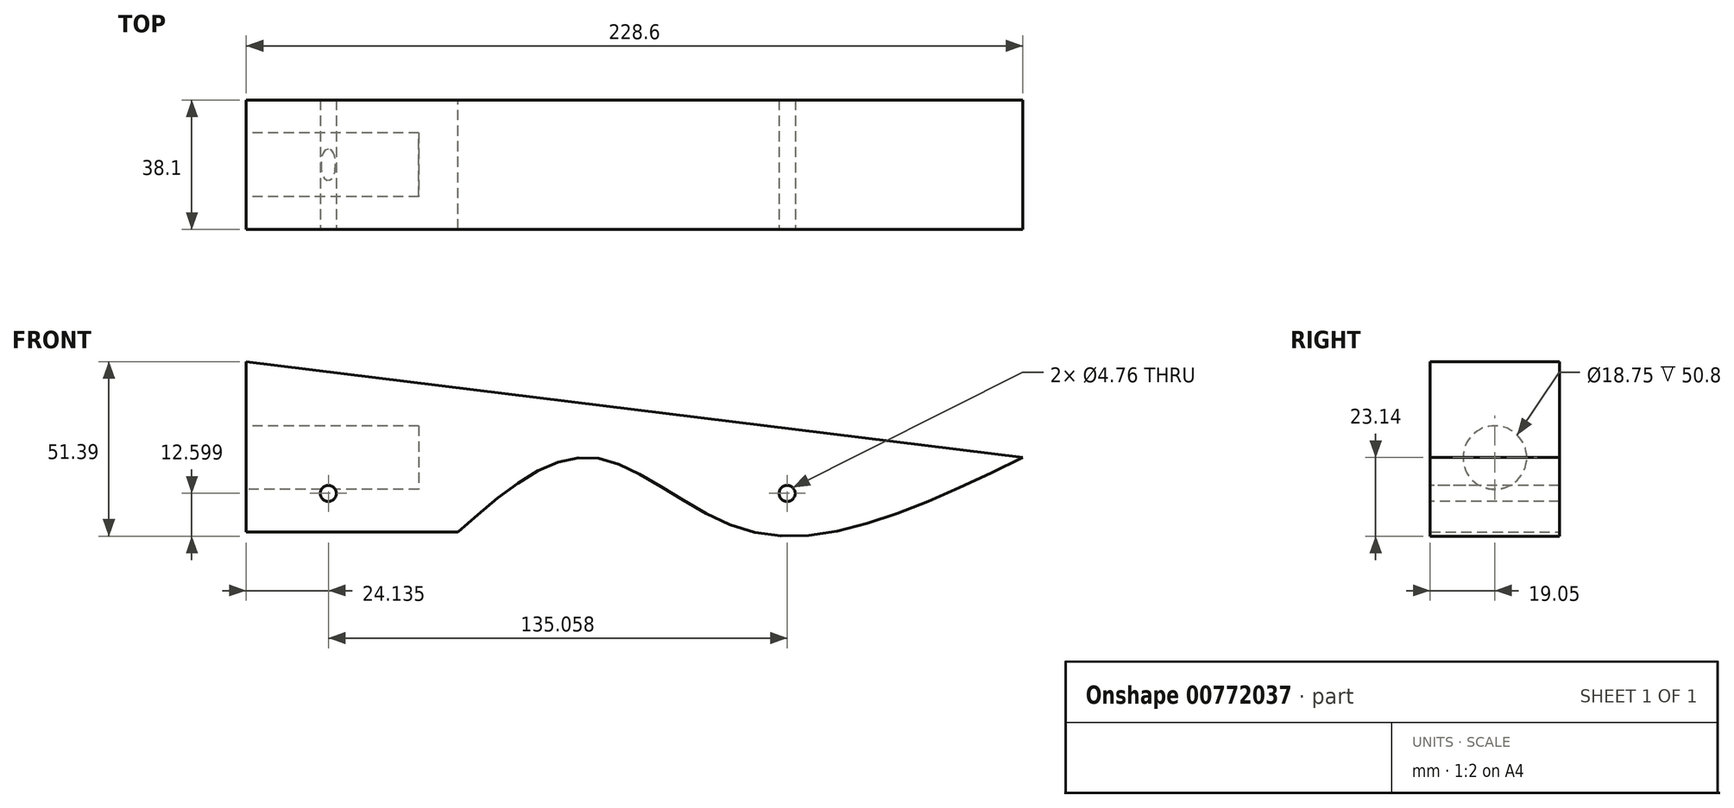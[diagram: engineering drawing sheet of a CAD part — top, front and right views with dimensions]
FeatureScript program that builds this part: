
annotation { "Feature Type Name" : "Feature", "Feature Type Description" : "" }
export const myFeature = defineFeature(function(context is Context, id is Id, definition is map)
    precondition{}
    {
        {
            var Q0;
            Q0=qCreatedBy(makeId("Front.planeOp"),FACE);
            var sketch = newSketch(context, id + "F0", { "sketchPlane" : qUnion([Q0])});
            skLineSegment(sketch, "E0", {"start": v(-66.4, 28.25) * mm, "end": v(-66.4, -21.94) * mm});
            skLineSegment(sketch, "E1", {"start": v(-66.4, -21.94) * mm, "end": v(-4.16, -21.94) * mm});
            skFitSpline(sketch, "E2", {"points": [v(-4.16, -21.94) * mm, v(35.7, 0) * mm, v(82.75, -21.94) * mm, v(162.2, 0) * mm], "startDerivative": vector(135.35, 119.24) * mm, "endDerivative": vector(215.58, 103.93) * mm});
            skLineSegment(sketch, "E3", {"start": v(-66.4, 28.25) * mm, "end": v(162.2, 0) * mm});
            skSolve(sketch);
        }
        {
            var Q0;
            Q0 = qSketchRegion(id + "F0", true);
            extrude(context, id + "F1", {"entities" : qUnion([Q0]), "depth" : 38.1 * mm, "offsetDistance" : 25.4 * mm});
        }
        {
            var Q0;
            Q0=makeQuery(id+"F1.opExtrude","CAP_FACE",FACE,{"disambiguationData":[OSD([sQuery(id+"F0.wireOp",EDGE,"E0"),sQuery(id+"F0.wireOp",EDGE,"E1"),sQuery(id+"F0.wireOp",EDGE,"E2"),sQuery(id+"F0.wireOp",EDGE,"E3")])],"isStart":false});
            var sketch = newSketch(context, id + "F2", { "sketchPlane" : qUnion([Q0])});
            skCircle(sketch, "E4", {"center": v(-42.27, -10.54) * mm, "radius": 2.38 * mm});
            skCircle(sketch, "E5", {"center": v(92.8, -10.54) * mm, "radius": 2.38 * mm});
            skSolve(sketch);
        }
        {
            var Q0;
            Q0=makeQuery(id+"F2.imprint","IMPRINT",FACE,{"disambiguationData":[TD([[makeQuery(id+"F2.imprint","IMPRINT",EDGE,{"derivedFrom":sQuery(id+"F2.wireOp",EDGE,"E5")}),1.0]])]});
            var Q1;
            Q1=makeQuery(id+"F2.imprint","IMPRINT",FACE,{"disambiguationData":[TD([[makeQuery(id+"F2.imprint","IMPRINT",EDGE,{"derivedFrom":sQuery(id+"F2.wireOp",EDGE,"E4")}),1.0]])]});
            extrude(context, id + "F3", {"entities" : qUnion([Q0, Q1]), "operationType" : NewBodyOperationType.REMOVE, "oppositeDirection" : true, "depth" : 50.8 * mm, "offsetDistance" : 25.4 * mm});
        }
        {
            var Q0;
            Q0=makeQuery(id+"F1.opExtrude","SWEPT_FACE",FACE,{"disambiguationData":[OSD([sQuery(id+"F0.wireOp",EDGE,"E0")])]});
            var sketch = newSketch(context, id + "F4", { "sketchPlane" : qUnion([Q0])});
            skCircle(sketch, "E6", {"center": v(19.05, 0) * mm, "radius": 9.37 * mm});
            skSolve(sketch);
        }
        {
            var Q0;
            Q0=makeQuery(id+"F4.imprint","IMPRINT",FACE,{"disambiguationData":[TD([[makeQuery(id+"F4.imprint","IMPRINT",EDGE,{"derivedFrom":sQuery(id+"F4.wireOp",EDGE,"E6")}),1.0]])]});
            extrude(context, id + "F5", {"entities" : qUnion([Q0]), "operationType" : NewBodyOperationType.REMOVE, "oppositeDirection" : true, "depth" : 50.8 * mm, "offsetDistance" : 25.4 * mm});
        }
    });
